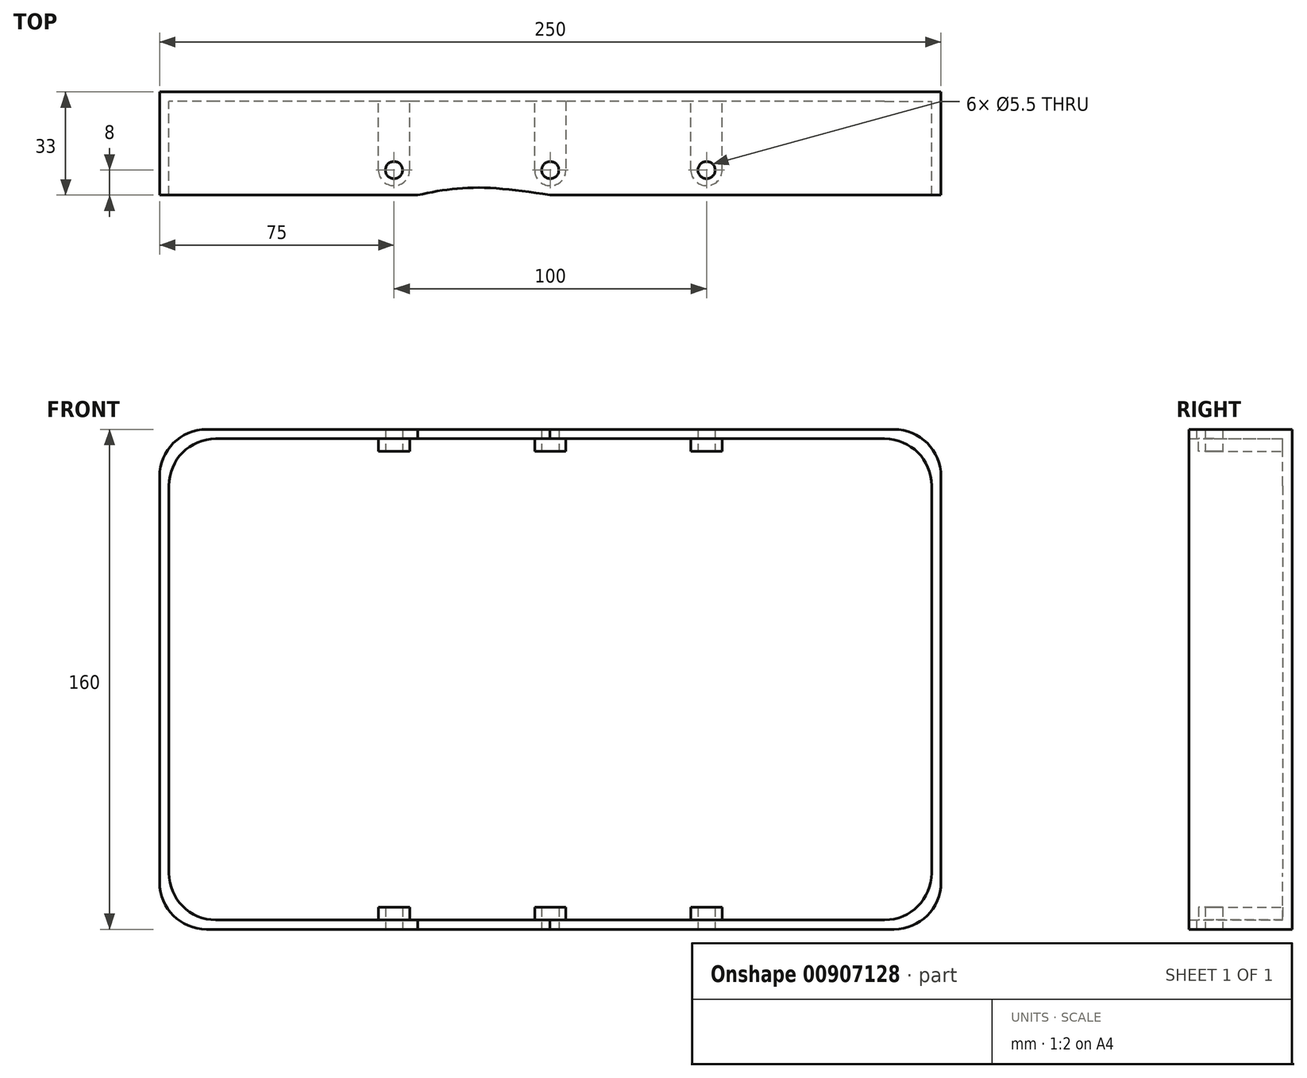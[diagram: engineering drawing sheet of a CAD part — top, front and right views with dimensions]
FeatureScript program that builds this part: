
annotation { "Feature Type Name" : "Feature", "Feature Type Description" : "" }
export const myFeature = defineFeature(function(context is Context, id is Id, definition is map)
    precondition{}
    {
        {
            var Q0;
            Q0=qCreatedBy(makeId("Front.planeOp"),FACE);
            var sketch = newSketch(context, id + "F0", { "sketchPlane" : qUnion([Q0])});
            skLineSegment(sketch, "E0.bottom", {"start": v(125, 80) * mm, "end": v(-125, 80) * mm});
            skLineSegment(sketch, "E0.top", {"start": v(125, -80) * mm, "end": v(-125, -80) * mm});
            skLineSegment(sketch, "E0.left", {"start": v(125, 80) * mm, "end": v(125, -80) * mm});
            skLineSegment(sketch, "E0.right", {"start": v(-125, 80) * mm, "end": v(-125, -80) * mm});
            skPoint(sketch, "E0.middle", {"position": v(0, 0) * mm});
            skSolve(sketch);
        }
        {
            var Q0;
            Q0=qSketchRegion(id+"F0",true);
            extrude(context, id + "F1", {"entities" : qUnion([Q0]), "depth" : 3 * mm, "offsetDistance" : 25 * mm});
        }
        {
            var Q0;
            Q0=makeQuery(id+"F1.opExtrude","CAP_FACE",FACE,{"disambiguationData":[OSD([sQuery(id+"F0.wireOp",EDGE,"E0.bottom"),sQuery(id+"F0.wireOp",EDGE,"E0.top"),sQuery(id+"F0.wireOp",EDGE,"E0.left"),sQuery(id+"F0.wireOp",EDGE,"E0.right")])],"isStart":false});
            var sketch = newSketch(context, id + "F2", { "sketchPlane" : qUnion([Q0])});
            skLineSegment(sketch, "E1.0", {"start": v(125, 80) * mm, "end": v(-125, 80) * mm});
            skLineSegment(sketch, "E2.0", {"start": v(-125, 80) * mm, "end": v(-125, -80) * mm});
            skLineSegment(sketch, "E3.0", {"start": v(125, -80) * mm, "end": v(-125, -80) * mm});
            skLineSegment(sketch, "E4.0", {"start": v(125, 80) * mm, "end": v(125, -80) * mm});
            skLineSegment(sketch, "E5.0", {"start": v(122, 77) * mm, "end": v(-122, 77) * mm});
            skLineSegment(sketch, "E6.0", {"start": v(-122, 77) * mm, "end": v(-122, -77) * mm});
            skLineSegment(sketch, "E7.0", {"start": v(122, -77) * mm, "end": v(-122, -77) * mm});
            skLineSegment(sketch, "E8", {"start": v(122, 77) * mm, "end": v(122, -77) * mm});
            skSolve(sketch);
        }
        {
            var Q0;
            Q0=makeQuery(id+"F2.imprint","IMPRINT",FACE,{"disambiguationData":[TD([[makeQuery(id+"F2.imprint","IMPRINT",EDGE,{"derivedFrom":sQuery(id+"F2.wireOp",EDGE,"E1.0")}),1.0]])]});
            extrude(context, id + "F3", {"entities" : qUnion([Q0]), "operationType" : NewBodyOperationType.ADD, "depth" : 30 * mm, "offsetDistance" : 25 * mm});
        }
        {
            var Q0;
            Q0=makeQuery(id+"F3.boolean.opBoolean","MERGE",FACE,{"derivedFrom":[makeQuery(id+"F1.opExtrude","SWEPT_FACE",FACE,{"disambiguationData":[OSD([sQuery(id+"F0.wireOp",EDGE,"E0.top")])]}),makeQuery(id+"F3.opExtrude","SWEPT_FACE",FACE,{"disambiguationData":[OSD([sQuery(id+"F2.wireOp",EDGE,"E3.0")])]})]});
            var sketch = newSketch(context, id + "F4", { "sketchPlane" : qUnion([Q0])});
            skCircle(sketch, "E9", {"center": v(0, 25) * mm, "radius": 2.75 * mm});
            skCircle(sketch, "E10", {"center": v(-50, 25) * mm, "radius": 2.75 * mm});
            skCircle(sketch, "E11", {"center": v(50, 25) * mm, "radius": 2.75 * mm});
            skSolve(sketch);
        }
        {
            var Q0;
            Q0=makeQuery(id+"F4.imprint","IMPRINT",FACE,{"disambiguationData":[TD([[makeQuery(id+"F4.imprint","IMPRINT",EDGE,{"derivedFrom":sQuery(id+"F4.wireOp",EDGE,"E9")}),1.0]])]});
            var Q1;
            Q1=makeQuery(id+"F4.imprint","IMPRINT",FACE,{"disambiguationData":[TD([[makeQuery(id+"F4.imprint","IMPRINT",EDGE,{"derivedFrom":sQuery(id+"F4.wireOp",EDGE,"E10")}),1.0]])]});
            var Q2;
            Q2=makeQuery(id+"F4.imprint","IMPRINT",FACE,{"disambiguationData":[TD([[makeQuery(id+"F4.imprint","IMPRINT",EDGE,{"derivedFrom":sQuery(id+"F4.wireOp",EDGE,"E11")}),1.0]])]});
            extrude(context, id + "F5", {"entities" : qUnion([Q0, Q1, Q2]), "operationType" : NewBodyOperationType.REMOVE, "endBound" : BoundingType.THROUGH_ALL, "oppositeDirection" : true, "depth" : 25 * mm, "offsetDistance" : 25 * mm});
        }
        {
            var Q0;
            Q0=makeQuery(id+"F3.boolean.opBoolean","MERGE",EDGE,{"derivedFrom":[makeQuery(id+"F1.opExtrude","SWEPT_EDGE",EDGE,{"disambiguationData":[OSD([sQuery(id+"F0.wireOp",EDGE,"E0.top"),sQuery(id+"F0.wireOp",EDGE,"E0.right")])]}),makeQuery(id+"F3.opExtrude","SWEPT_EDGE",EDGE,{"disambiguationData":[OSD([sQuery(id+"F2.wireOp",EDGE,"E2.0"),sQuery(id+"F2.wireOp",EDGE,"E3.0")])]})]});
            var Q1;
            Q1=makeQuery(id+"F3.boolean.opBoolean","MERGE",EDGE,{"derivedFrom":[makeQuery(id+"F1.opExtrude","SWEPT_EDGE",EDGE,{"disambiguationData":[OSD([sQuery(id+"F0.wireOp",EDGE,"E0.bottom"),sQuery(id+"F0.wireOp",EDGE,"E0.right")])]}),makeQuery(id+"F3.opExtrude","SWEPT_EDGE",EDGE,{"disambiguationData":[OSD([sQuery(id+"F2.wireOp",EDGE,"E1.0"),sQuery(id+"F2.wireOp",EDGE,"E2.0")])]})]});
            var Q2;
            Q2=makeQuery(id+"F3.boolean.opBoolean","MERGE",EDGE,{"derivedFrom":[makeQuery(id+"F1.opExtrude","SWEPT_EDGE",EDGE,{"disambiguationData":[OSD([sQuery(id+"F0.wireOp",EDGE,"E0.bottom"),sQuery(id+"F0.wireOp",EDGE,"E0.left")])]}),makeQuery(id+"F3.opExtrude","SWEPT_EDGE",EDGE,{"disambiguationData":[OSD([sQuery(id+"F2.wireOp",EDGE,"E1.0"),sQuery(id+"F2.wireOp",EDGE,"E4.0")])]})]});
            var Q3;
            Q3=makeQuery(id+"F3.boolean.opBoolean","MERGE",EDGE,{"derivedFrom":[makeQuery(id+"F1.opExtrude","SWEPT_EDGE",EDGE,{"disambiguationData":[OSD([sQuery(id+"F0.wireOp",EDGE,"E0.top"),sQuery(id+"F0.wireOp",EDGE,"E0.left")])]}),makeQuery(id+"F3.opExtrude","SWEPT_EDGE",EDGE,{"disambiguationData":[OSD([sQuery(id+"F2.wireOp",EDGE,"E3.0"),sQuery(id+"F2.wireOp",EDGE,"E4.0")])]})]});
            var Q4;
            Q4=makeQuery(id+"F3.opExtrude","SWEPT_EDGE",EDGE,{"disambiguationData":[OSD([sQuery(id+"F2.wireOp",EDGE,"E5.0"),sQuery(id+"F2.wireOp",EDGE,"E8")])]});
            var Q5;
            Q5=makeQuery(id+"F3.opExtrude","SWEPT_EDGE",EDGE,{"disambiguationData":[OSD([sQuery(id+"F2.wireOp",EDGE,"E5.0"),sQuery(id+"F2.wireOp",EDGE,"E6.0")])]});
            var Q6;
            Q6=makeQuery(id+"F3.opExtrude","SWEPT_EDGE",EDGE,{"disambiguationData":[OSD([sQuery(id+"F2.wireOp",EDGE,"E6.0"),sQuery(id+"F2.wireOp",EDGE,"E7.0")])]});
            var Q7;
            Q7=makeQuery(id+"F3.opExtrude","SWEPT_EDGE",EDGE,{"disambiguationData":[OSD([sQuery(id+"F2.wireOp",EDGE,"E7.0"),sQuery(id+"F2.wireOp",EDGE,"E8")])]});
            fillet(context, id + "F6", {"entities" : qUnion([Q0, Q1, Q2, Q3, Q4, Q5, Q6, Q7]), "radius" : 15 * mm, "tangentPropagation" : true, "allowEdgeOverflow" : false});
        }
        {
            var Q0;
            Q0=makeQuery(id+"F4.imprint","IMPRINT",FACE,{"disambiguationData":[TD([[makeQuery(id+"F4.imprint","IMPRINT",EDGE,{"derivedFrom":sQuery(id+"F4.wireOp",EDGE,"E9")}),-1.0]])]});
            var sketch = newSketch(context, id + "F7", { "sketchPlane" : qUnion([Q0])});
            skFitSpline(sketch, "E12", {"points": [v(-161.6, 24.56) * mm, v(-113.27, 38.05) * mm, v(-54.94, 35.87) * mm, v(-21, 30.65) * mm, v(46.92, 38.49) * mm, v(123.53, 27.17) * mm, v(174.02, 33.26) * mm, v(165.32, 75.92) * mm, v(77.39, 101.17) * mm, v(70.42, 102.04) * mm, v(-44.93, 102.04) * mm, v(-113.27, 90.72) * mm, v(-179.44, 44.58) * mm, v(-161.6, 24.56) * mm]});
            skSolve(sketch);
        }
        {
            var Q0;
            {var subQ1=sQuery(id+"F2.wireOp",EDGE,"E3.0");var subQ7=makeQuery(id+"F4.imprint","IMPRINT",EDGE,{"derivedFrom":makeQuery(id+"F3.opExtrude","CAP_EDGE",EDGE,{"disambiguationData":[OSD([subQ1])],"isStart":false})});Q0=makeQuery(id+"F7.imprint","IMPRINT",FACE,{"disambiguationData":[TD([[makeQuery(id+"F7.imprint","IMPRINT",EDGE,{"derivedFrom":subQ7}),-1.0]])]});}
            var Q1;
            {var subQ1=sQuery(id+"F2.wireOp",EDGE,"E3.0");var subQ7=makeQuery(id+"F4.imprint","IMPRINT",EDGE,{"derivedFrom":makeQuery(id+"F3.opExtrude","CAP_EDGE",EDGE,{"disambiguationData":[OSD([subQ1])],"isStart":false})});Q1=makeQuery(id+"F7.imprint","IMPRINT",FACE,{"disambiguationData":[TD([[makeQuery(id+"F7.imprint","IMPRINT",EDGE,{"derivedFrom":subQ7}),1.0]])]});}
            extrude(context, id + "F8", {"entities" : qUnion([Q0, Q1]), "operationType" : NewBodyOperationType.REMOVE, "endBound" : BoundingType.THROUGH_ALL, "oppositeDirection" : true, "depth" : 25 * mm, "offsetDistance" : 25 * mm});
        }
        {
            var Q0;
            Q0=makeQuery(id+"F3.opExtrude","SWEPT_FACE",FACE,{"disambiguationData":[OSD([sQuery(id+"F2.wireOp",EDGE,"E5.0")])]});
            var sketch = newSketch(context, id + "F9", { "sketchPlane" : qUnion([Q0])});
            skArc(sketch, "E13", {"start": v(-45, 25) * mm, "mid": v(-50, 30) * mm, "end": v(-55, 25) * mm});
            skArc(sketch, "E14", {"start": v(5, 25) * mm, "mid": v(0, 30) * mm, "end": v(-5, 25) * mm});
            skArc(sketch, "E15", {"start": v(55, 25) * mm, "mid": v(50, 30) * mm, "end": v(45, 25) * mm});
            skCircle(sketch, "E16.0", {"center": v(0, 25) * mm, "radius": 2.75 * mm});
            skCircle(sketch, "E17.0", {"center": v(50, 25) * mm, "radius": 2.75 * mm});
            skCircle(sketch, "E18.0", {"center": v(-50, 25) * mm, "radius": 2.75 * mm});
            skLineSegment(sketch, "E19", {"start": v(-45, 25) * mm, "end": v(-45, 3) * mm});
            skLineSegment(sketch, "E20", {"start": v(-55, 25) * mm, "end": v(-55, 3) * mm});
            skLineSegment(sketch, "E21", {"start": v(-55, 3) * mm, "end": v(-45, 3) * mm});
            skLineSegment(sketch, "E22", {"start": v(-45, 3) * mm, "end": v(-55, 3) * mm});
            skLineSegment(sketch, "E23", {"start": v(-5, 25.08) * mm, "end": v(-5, 3) * mm});
            skLineSegment(sketch, "E24", {"start": v(-5, 3) * mm, "end": v(5, 3) * mm});
            skLineSegment(sketch, "E25", {"start": v(5, 3) * mm, "end": v(5, 25) * mm});
            skLineSegment(sketch, "E26", {"start": v(45, 25) * mm, "end": v(45, 3) * mm});
            skLineSegment(sketch, "E27", {"start": v(55, 25.08) * mm, "end": v(55, 3) * mm});
            skLineSegment(sketch, "E28", {"start": v(55, 3) * mm, "end": v(45, 3) * mm});
            skSolve(sketch);
        }
        {
            var Q0;
            Q0=qSketchRegion(id+"F9",true);
            extrude(context, id + "F10", {"entities" : qUnion([Q0]), "operationType" : NewBodyOperationType.ADD, "depth" : 4 * mm, "offsetDistance" : 25 * mm});
        }
        {
            var Q0;
            Q0=makeQuery(id+"F3.opExtrude","SWEPT_FACE",FACE,{"disambiguationData":[OSD([sQuery(id+"F2.wireOp",EDGE,"E7.0")])]});
            var sketch = newSketch(context, id + "F11", { "sketchPlane" : qUnion([Q0])});
            skArc(sketch, "E29.0", {"start": v(-45, -25) * mm, "mid": v(-50, -30) * mm, "end": v(-55, -25) * mm});
            skLineSegment(sketch, "E30.0", {"start": v(-55, -25) * mm, "end": v(-55, -3) * mm});
            skLineSegment(sketch, "E31.0", {"start": v(-45, -25) * mm, "end": v(-45, -3) * mm});
            skLineSegment(sketch, "E32.0", {"start": v(-45, -3) * mm, "end": v(-55, -3) * mm});
            skLineSegment(sketch, "E33.0.2", {"start": v(-55, -3) * mm, "end": v(-45, -3) * mm});
            skLineSegment(sketch, "E33.0.3", {"start": v(-45, -3) * mm, "end": v(-45, -25) * mm});
            skLineSegment(sketch, "E34.0.0", {"start": v(-5, -3) * mm, "end": v(5, -3) * mm});
            skLineSegment(sketch, "E34.0.1", {"start": v(5, -3) * mm, "end": v(5, -25) * mm});
            skArc(sketch, "E34.0.2", {"start": v(5, -25) * mm, "mid": v(0, -30) * mm, "end": v(-5, -25) * mm});
            skLineSegment(sketch, "E34.0.3", {"start": v(-5, -25) * mm, "end": v(-5, -3) * mm});
            skLineSegment(sketch, "E35.0.0", {"start": v(55, -3) * mm, "end": v(55, -25) * mm});
            skArc(sketch, "E35.0.1", {"start": v(55, -25) * mm, "mid": v(50, -30) * mm, "end": v(45, -25) * mm});
            skLineSegment(sketch, "E35.0.2", {"start": v(45, -25) * mm, "end": v(45, -3) * mm});
            skLineSegment(sketch, "E35.0.3", {"start": v(45, -3) * mm, "end": v(55, -3) * mm});
            skCircle(sketch, "E36.0", {"center": v(-50, -25) * mm, "radius": 2.75 * mm});
            skCircle(sketch, "E37.0", {"center": v(0, -25) * mm, "radius": 2.75 * mm});
            skCircle(sketch, "E37.1", {"center": v(50, -25) * mm, "radius": 2.75 * mm});
            skSolve(sketch);
        }
        {
            var Q0;
            Q0=qSketchRegion(id+"F11",true);
            extrude(context, id + "F12", {"entities" : qUnion([Q0]), "operationType" : NewBodyOperationType.ADD, "depth" : 4 * mm, "offsetDistance" : 25 * mm});
        }
    });
